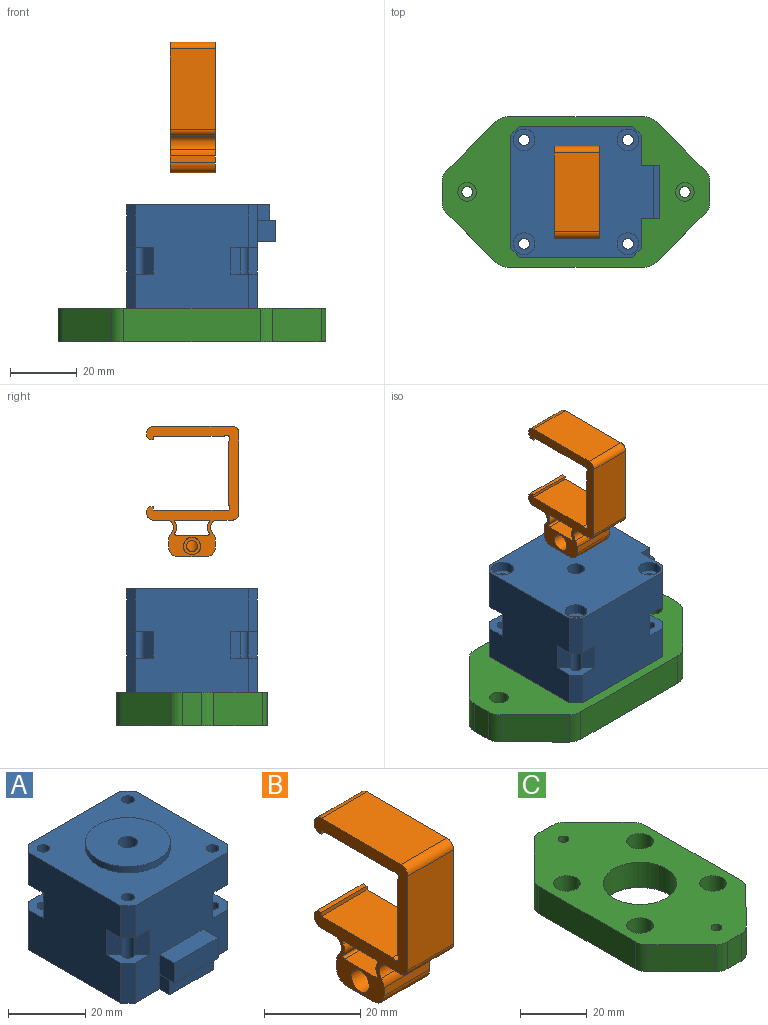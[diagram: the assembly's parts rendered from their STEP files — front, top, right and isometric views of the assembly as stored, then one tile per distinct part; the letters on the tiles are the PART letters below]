
ASSEMBLY  parts=3 mates=2
PART A: 53 faces, bbox 39x44.5x32.9 mm
  f0: plane 8x2.78mm, normal (0.71,-0.71,0), area 31.4mm2, adj f8,f27,f28,f50
  f1: plane 8x2.78mm, normal (0.71,-0.71,0), area 31.4mm2, adj f13,f27,f28,f50
  f2: plane 8x2.78mm, normal (0.71,0.71,0), area 31.4mm2, adj f13,f31,f32,f47
  f3: plane 8x2.78mm, normal (0.71,0.71,0), area 31.4mm2, adj f14,f31,f32,f47
  f4: plane 8x2.78mm, normal (-0.71,0.71,0), area 31.4mm2, adj f14,f29,f30,f44
  f5: plane 8x2.78mm, normal (-0.71,0.71,0), area 31.4mm2, adj f15,f29,f30,f44
  f6: plane 8x2.78mm, normal (-0.71,-0.71,0), area 31.4mm2, adj f15,f25,f26,f41
  f7: plane 8x2.78mm, normal (-0.71,-0.71,0), area 31.4mm2, adj f8,f25,f26,f41
  f8: plane 33.83x30.85mm, normal (0,-1,0), area 784.9mm2, adj f0,f7,f11,f12,f19,f22,f23,f24
  f9: plane 12.65x2.58mm, normal (0.71,0.71,0), area 46.2mm2, adj f13,f14,f19,f32
  f10: plane 12.65x2.58mm, normal (-0.71,0.71,0), area 46.2mm2, adj f14,f15,f19,f30
  f11: plane 12.65x2.58mm, normal (-0.71,-0.71,0), area 46.2mm2, adj f8,f15,f19,f26
  f12: plane 12.65x2.58mm, normal (0.71,-0.71,0), area 46.2mm2, adj f8,f13,f19,f28
  f13: plane 33.83x30.85mm, normal (1,0,0), area 958.9mm2, adj f1,f2,f9,f12,f19,f20,f23,f24
  f14: plane 33.83x30.85mm, normal (0,1,0), area 958.9mm2, adj f3,f4,f9,f10,f19,f20,f21,f24
  f15: plane 33.83x30.85mm, normal (-1,0,0), area 958.9mm2, adj f5,f6,f10,f11,f19,f21,f22,f24
  f16: cylinder r=2.5mm len=32.85mm, axis (0,0,-1), area 516mm2, adj f18,f19
  f17: cylinder r=11mm len=22mm, axis (0,0,-1), area 138.2mm2, adj f18,f24
  f18: plane 22x22mm, normal (0,0,1), area 360.5mm2, adj f16,f17
  f19: plane 42.75x39mm, normal (0,0,-1), area 1414.9mm2, adj f8,f9,f10,f11,f12,f13,f14,f15
  f20: plane 10.2x2.58mm, normal (0.71,0.71,0), area 37.3mm2, adj f13,f14,f24,f31
  f21: plane 10.2x2.58mm, normal (-0.71,0.71,0), area 37.3mm2, adj f14,f15,f24,f29
  f22: plane 10.2x2.58mm, normal (-0.71,-0.71,0), area 37.3mm2, adj f8,f15,f24,f25
  f23: plane 10.2x2.58mm, normal (0.71,-0.71,0), area 37.3mm2, adj f8,f13,f24,f27
  f24: plane 39x39mm, normal (0,0,1), area 1093.3mm2, adj f8,f13,f14,f15,f17,f20,f21,f22
  f25: plane 7.89x7.89mm, normal (0,0,-1), area 23.8mm2, adj f6,f7,f8,f15,f22,f41
  f26: plane 7.89x7.89mm, normal (0,0,1), area 23.8mm2, adj f6,f7,f8,f11,f15,f41
  f27: plane 7.89x7.89mm, normal (0,0,-1), area 23.8mm2, adj f0,f1,f8,f13,f23,f50
  f28: plane 7.89x7.89mm, normal (0,0,1), area 23.8mm2, adj f0,f1,f8,f12,f13,f50
  f29: plane 7.89x7.89mm, normal (0,0,-1), area 23.8mm2, adj f4,f5,f14,f15,f21,f44
  f30: plane 7.89x7.89mm, normal (0,0,1), area 23.8mm2, adj f4,f5,f10,f14,f15,f44
  f31: plane 7.89x7.89mm, normal (0,0,-1), area 23.8mm2, adj f2,f3,f13,f14,f20,f47
  f32: plane 7.89x7.89mm, normal (0,0,1), area 23.8mm2, adj f2,f3,f9,f13,f14,f47
  f33: plane 4.6x3.75mm, normal (1,0,0), area 17.2mm2, adj f8,f19,f35,f37
  f34: plane 4.6x3.75mm, normal (-1,0,0), area 17.2mm2, adj f8,f19,f35,f37
  f35: plane 15.9x4.6mm, normal (0,-1,0), area 73.1mm2, adj f19,f33,f34,f37
  f36: plane 6.3x5.5mm, normal (-1,0,0), area 34.6mm2, adj f8,f37,f39,f40
  f37: plane 16x5.5mm, normal (0,0,-1), area 28.4mm2, adj f8,f33,f34,f35,f36,f38,f40
  f38: plane 6.3x5.5mm, normal (1,0,0), area 34.6mm2, adj f8,f37,f39,f40
  f39: plane 16x5.5mm, normal (0,0,1), area 88mm2, adj f8,f36,f38,f40
  f40: plane 16x6.3mm, normal (0,-1,0), area 100.8mm2, adj f36,f37,f38,f39
  f41: cylinder r=1.65mm len=27.85mm, axis (0,0,-1), area 248.5mm2, adj f6,f7,f24,f25,f26,f42
  f42: plane 6.5x6.5mm, normal (0,0,-1), area 24.6mm2, adj f41,f43
  f43: cylinder r=3.25mm len=6.5mm, axis (0,0,-1), area 61.3mm2, adj f19,f42
  f44: cylinder r=1.65mm len=27.85mm, axis (0,0,-1), area 248.5mm2, adj f4,f5,f24,f29,f30,f45
  f45: plane 6.5x6.5mm, normal (0,0,-1), area 24.6mm2, adj f44,f46
  f46: cylinder r=3.25mm len=6.5mm, axis (0,0,-1), area 61.3mm2, adj f19,f45
  f47: cylinder r=1.65mm len=27.85mm, axis (0,0,-1), area 248.5mm2, adj f2,f3,f24,f31,f32,f48
  f48: plane 6.5x6.5mm, normal (0,0,-1), area 24.6mm2, adj f47,f49
  f49: cylinder r=3.25mm len=6.5mm, axis (0,0,-1), area 61.3mm2, adj f19,f48
  f50: cylinder r=1.65mm len=27.85mm, axis (0,0,-1), area 248.5mm2, adj f0,f1,f24,f27,f28,f51
  f51: plane 6.5x6.5mm, normal (0,0,-1), area 24.6mm2, adj f50,f52
  f52: cylinder r=3.25mm len=6.5mm, axis (0,0,-1), area 61.3mm2, adj f19,f51
PART B: 44 faces, bbox 13.5x27.5x39 mm
  f0: plane 13.49x9.31mm, normal (0,0,1), area 113mm2, adj f1,f3,f5,f32,f34
  f1: cylinder r=2mm len=6.5mm, axis (0,0,-1), area 72.1mm2, adj f0,f6,f7
  f2: plane 13.49x2.07mm, normal (0,1,0), area 28mm2, adj f3,f5,f41,f43
  f3: plane 39x27.5mm, normal (-1,0,0), area 304.8mm2, adj f0,f2,f4,f6,f9,f10,f11,f12
  f4: plane 13.49x2.07mm, normal (0,-1,0), area 28mm2, adj f3,f5,f40,f42
  f5: plane 39x27.5mm, normal (1,0,0), area 326.4mm2, adj f0,f2,f4,f6,f10,f11,f12,f13
  f6: plane 13.49x8mm, normal (0,0,-1), area 95.3mm2, adj f1,f3,f5,f40,f41
  f7: cylinder r=1.65mm len=3.3mm, axis (-1,0,0), area 11.3mm2, adj f1,f8
  f8: plane 5.05x5.05mm, normal (-1,0,0), area 11.5mm2, adj f7,f9
  f9: cone r=2.52mm half-angle=1.5deg, axis (-1,0,0), area 61.5mm2, adj f3,f8
  f10: cylinder r=2.5mm len=13.49mm, axis (-1,0,0), area 62.5mm2, adj f3,f5,f11,f43
  f11: plane 13.49x4.5mm, normal (0,0,-1), area 60.7mm2, adj f3,f5,f10,f36
  f12: plane 13.49x1mm, normal (0,1,0), area 13.5mm2, adj f3,f5,f13,f36
  f13: plane 13.49x1mm, normal (0,0.77,0.64), area 17.6mm2, adj f3,f5,f12,f14
  f14: plane 13.49x1.16mm, normal (0,0,1), area 15.7mm2, adj f3,f5,f13,f15
  f15: plane 13.49x1mm, normal (0,-1,0), area 13.5mm2, adj f3,f5,f14,f16
  f16: plane 21.09x13.49mm, normal (0,0,1), area 284.4mm2, adj f3,f5,f15,f17
  f17: cylinder r=1mm len=13.49mm, axis (-1,0,0), area 42.4mm2, adj f3,f5,f16,f18
  f18: plane 19.17x13.49mm, normal (0,1,0), area 258.6mm2, adj f3,f5,f17,f19
  f19: cylinder r=1mm len=13.49mm, axis (-1,0,0), area 42.4mm2, adj f3,f5,f18,f20
  f20: plane 21.09x13.49mm, normal (0,0,-1), area 284.4mm2, adj f3,f5,f19,f21
  f21: plane 13.49x1mm, normal (0,-1,0), area 13.5mm2, adj f3,f5,f20,f22
  f22: plane 13.49x1.16mm, normal (0,0,-1), area 15.7mm2, adj f3,f5,f21,f23
  f23: plane 13.49x1mm, normal (0,0.77,-0.64), area 17.6mm2, adj f3,f5,f22,f24
  f24: plane 13.49x1mm, normal (0,1,0), area 13.5mm2, adj f3,f5,f23,f37
  f25: plane 23.5x13.49mm, normal (0,0,1), area 317mm2, adj f3,f5,f37,f38
  f26: plane 24x13.49mm, normal (0,-1,0), area 323.7mm2, adj f3,f5,f38,f39
  f27: plane 13.49x5mm, normal (0,0,-1), area 67.4mm2, adj f3,f5,f28,f39
  f28: cylinder r=2.5mm len=13.49mm, axis (-1,0,0), area 62.5mm2, adj f3,f5,f27,f42
  f29: cylinder r=2.5mm len=13.49mm, axis (-1,0,0), area 42mm2, adj f3,f5,f32,f33
  f30: plane 13.49x9.31mm, normal (0,0,-1), area 125.5mm2, adj f3,f5,f33,f35
  f31: cylinder r=2.5mm len=13.49mm, axis (-1,0,0), area 42mm2, adj f3,f5,f34,f35
  f32: cylinder r=0.5mm len=13.49mm, axis (-1,0,0), area 14.8mm2, adj f0,f3,f5,f29
  f33: cylinder r=0.5mm len=13.49mm, axis (-1,0,0), area 14.8mm2, adj f3,f5,f29,f30
  f34: cylinder r=0.5mm len=13.49mm, axis (-1,0,0), area 14.8mm2, adj f0,f3,f5,f31
  f35: cylinder r=0.5mm len=13.49mm, axis (-1,0,0), area 14.8mm2, adj f3,f5,f30,f31
  f36: cylinder r=2mm len=13.49mm, axis (1,0,0), area 42.4mm2, adj f3,f5,f11,f12
  f37: cylinder r=2mm len=13.49mm, axis (1,0,0), area 42.4mm2, adj f3,f5,f24,f25
  f38: cylinder r=2mm len=13.49mm, axis (-1,0,0), area 42.4mm2, adj f3,f5,f25,f26
  f39: cylinder r=2mm len=13.49mm, axis (1,0,0), area 42.4mm2, adj f3,f5,f26,f27
  f40: cylinder r=3mm len=13.49mm, axis (1,0,0), area 63.6mm2, adj f3,f4,f5,f6
  f41: cylinder r=3mm len=13.49mm, axis (-1,0,0), area 63.6mm2, adj f2,f3,f5,f6
  f42: cylinder r=3mm len=13.49mm, axis (-1,0,0), area 29.6mm2, adj f3,f4,f5,f28
  f43: cylinder r=3mm len=13.49mm, axis (-1,0,0), area 29.6mm2, adj f2,f3,f5,f10
PART C: 38 faces, bbox 45x80x10 mm
  f0: cylinder r=1.65mm len=4mm, axis (0,0,-1), area 41.5mm2, adj f14,f21
  f1: cylinder r=1.65mm len=4mm, axis (0,0,-1), area 41.5mm2, adj f14,f19
  f2: cylinder r=1.65mm len=4mm, axis (0,0,-1), area 41.5mm2, adj f14,f17
  f3: cylinder r=1.65mm len=4mm, axis (0,0,-1), area 41.5mm2, adj f14,f15
  f4: plane 14.57x14.57mm, normal (-0.71,-0.71,0), area 206.1mm2, adj f13,f14,f30,f37
  f5: plane 10x5.86mm, normal (0,-1,0), area 58.6mm2, adj f13,f14,f30,f31
  f6: plane 14.57x14.57mm, normal (0.71,-0.71,0), area 206.1mm2, adj f13,f14,f31,f32
  f7: plane 40.86x10mm, normal (1,0,0), area 408.6mm2, adj f13,f14,f32,f33
  f8: plane 14.57x14.57mm, normal (0.71,0.71,0), area 206.1mm2, adj f13,f14,f33,f34
  f9: plane 10x5.86mm, normal (0,1,0), area 58.6mm2, adj f13,f14,f34,f35
  f10: plane 14.57x14.57mm, normal (-0.71,0.71,0), area 206.1mm2, adj f13,f14,f35,f36
  f11: cylinder r=11mm len=22mm, axis (0,0,-1), area 622mm2, adj f13,f29
  f12: plane 40.86x10mm, normal (-1,0,0), area 408.6mm2, adj f13,f14,f36,f37
  f13: plane 80x45mm, normal (0,0,1), area 2385.3mm2, adj f4,f5,f6,f7,f8,f9,f10,f11
  f14: plane 80x45mm, normal (0,0,-1), area 2448.1mm2, adj f0,f1,f2,f3,f4,f5,f6,f7
  f15: plane 8x8mm, normal (0,0,1), area 41.7mm2, adj f3,f16
  f16: cylinder r=4mm len=8mm, axis (0,0,1), area 150.8mm2, adj f13,f15
  f17: plane 8x8mm, normal (0,0,1), area 41.7mm2, adj f2,f18
  f18: cylinder r=4mm len=8mm, axis (0,0,1), area 150.8mm2, adj f13,f17
  f19: plane 8x8mm, normal (0,0,1), area 41.7mm2, adj f1,f20
  f20: cylinder r=4mm len=8mm, axis (0,0,1), area 150.8mm2, adj f13,f19
  f21: plane 8x8mm, normal (0,0,1), area 41.7mm2, adj f0,f22
  f22: cylinder r=4mm len=8mm, axis (0,0,1), area 150.8mm2, adj f13,f21
  f23: cylinder r=1.63mm len=3.26mm, axis (0,0,-1), area 20.5mm2, adj f13,f24
  f24: plane 5.56x5.56mm, normal (0,0,-1), area 15.9mm2, adj f23,f25
  f25: cylinder r=2.78mm len=8mm, axis (0,0,-1), area 139.6mm2, adj f14,f24
  f26: cylinder r=1.63mm len=3.26mm, axis (0,0,-1), area 20.5mm2, adj f13,f27
  f27: plane 5.56x5.56mm, normal (0,0,-1), area 15.9mm2, adj f26,f28
  f28: cylinder r=2.78mm len=8mm, axis (0,0,-1), area 139.6mm2, adj f14,f27
  f29: cone r=12mm half-angle=45deg, axis (0,0,-1), area 102.2mm2, adj f11,f14
  f30: cylinder r=5mm len=10mm, axis (0,0,-1), area 39.3mm2, adj f4,f5,f13,f14
  f31: cylinder r=5mm len=10mm, axis (0,0,1), area 39.3mm2, adj f5,f6,f13,f14
  f32: cylinder r=5mm len=10mm, axis (0,0,1), area 39.3mm2, adj f6,f7,f13,f14
  f33: cylinder r=5mm len=10mm, axis (0,0,-1), area 39.3mm2, adj f7,f8,f13,f14
  f34: cylinder r=5mm len=10mm, axis (0,0,1), area 39.3mm2, adj f8,f9,f13,f14
  f35: cylinder r=5mm len=10mm, axis (0,0,-1), area 39.3mm2, adj f9,f10,f13,f14
  f36: cylinder r=5mm len=10mm, axis (0,0,-1), area 39.3mm2, adj f10,f12,f13,f14
  f37: cylinder r=5mm len=10mm, axis (0,0,1), area 39.3mm2, adj f4,f12,f13,f14
PLACE A rot(axis=(0.71,-0.71,0),180deg) t=(-272.5,-57.02,-18.02)mm
PLACE B t=(-272.5,-57.02,-5.21)mm
PLACE C rot(axis=(0.71,-0.71,0),180deg) t=(-272.5,-57.02,-18.02)mm
MATE slider A.f16 <-> B.f1  axis (0,0,1) through (-272.5,-57.02,-18.02)mm
MATE fastened A.f16 <-> C.f11  axis (0,0,-1) through (-272.5,-57.02,-48.87)mm
